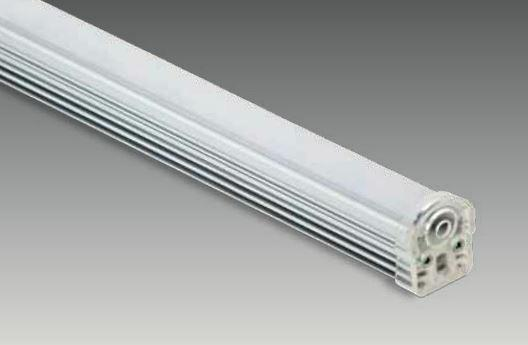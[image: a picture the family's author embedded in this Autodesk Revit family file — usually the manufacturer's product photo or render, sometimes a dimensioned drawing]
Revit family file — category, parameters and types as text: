
# Revit family: SD 1245 CVK
name_source: partatom
category: Lighting Fixtures
revit_build: Autodesk Revit 2017 (Build: 20160225_1515(x64)
units: mm (PartAtom-declared; Revit-internal decimal feet)

## family parameters
Cut with Voids When Loaded = No
Host = Face
Light Source = Yes
Part Type = Normal
Room Calculation Point = No
Round Connector Dimension = Use Diameter
Shared = No

## types (2) — shared parameters
Apparent Load = 30 VA
Color Filter = 16777215
Default Elevation = 1219 mm
Dimming Lamp Color Temperature Shift = <None>
Emit Shape Visible in Rendering = Yes
Emit from Rectangle Length = 15 mm  [stored 0.0492126 ft]
Emit from Rectangle Width = 1245 mm
Light Source Symbol Size = 610 mm
Manufacturer = ARLIGHT
Type Image = SD 1245 CVK.JPG
Wattage Comments = 30

## type names (no varying parameters)
- SDCVK.1245.30.30
- SDCVK.1245.30.40

note: [stored X ft] marks values corroborated as IEEE doubles in the binary element streams (Revit-internal decimal feet)

## geometry (parser evidence)
native form markers: Sweep x3
no freeform markers — native parametric forms only
